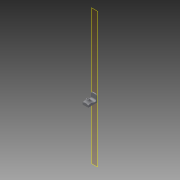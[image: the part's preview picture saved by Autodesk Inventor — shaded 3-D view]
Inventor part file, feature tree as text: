
AUTODESK INVENTOR PART (.ipt)
format: ipt  version: 2015 (Build 190159000, 159)  size: 176,640 bytes
history: native  units: in
note: dims shown in document units (in); Inventor stores cm internally (conversion verified against a paired STEP export)
features: extrude x6, sketch x6, reference x4, fillet x3, plane x1, projected_geometry x1
ambient origin geometry x8: Origin, YZ Plane, XZ Plane, XY Plane, X Axis, Y Axis, Z Axis, Center Point
bodies: Solid1 (feature_tree)
feature tree (21):
  plane  "Work Plane1"
  extrude  "Extrusion1"  Depth=0.2in
  extrude  "Extrusion2"  Depth=0.15in
  extrude  "Extrusion3"  Depth=0.5in TaperAngle=0.0deg
  fillet  "Fillet1"  Radius=0.5in
  fillet  "Fillet2"  Radius=0.1875in
  fillet  "Fillet3"  Radius=0.1875in
  extrude  "Extrusion4"  Depth=0.5in
  extrude  "Extrusion5"  Depth=0.5in TaperAngle=0.0deg
  extrude  "Extrusion6"  [1 undecoded]
  sketch  "Sketch1"  dims[d0=1.0in d1=0.2in]
  reference  "Reference1"
  reference  "Reference2"
  sketch  "Sketch2"  dims[d2=0.125in d3=0.0in d4=0.15in]
  sketch  "Sketch3"  dims[d5=1.25in d6=0.0in d7=0.5in d8=0.0in d9=0.5in d10=0.1875in d11=0.1875in]
  reference  "Reference3"
  sketch  "Sketch5"  dims[d14=0.5in d15=0.0in d16=0.1406in]
  projected_geometry  "Projected Loop1"
  sketch  "Sketch6"  dims[d17=0.1406in d18=0.5in d19=0.0in]
  sketch  "Sketch7"  dims[d20=0.5in d21=0.0in]
  reference  "Reference4"
note: 1 required parameter value undecoded (feature->parameter linkage not recoverable at this tier; creation-order binding heuristic only, values carry confidence <= 0.55)
